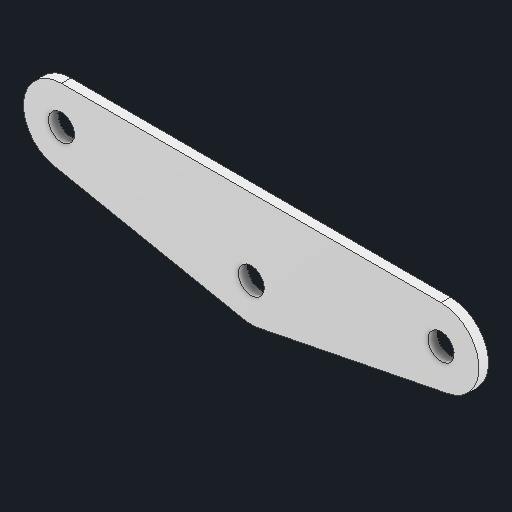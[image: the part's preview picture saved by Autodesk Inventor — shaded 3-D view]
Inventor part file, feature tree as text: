
AUTODESK INVENTOR PART (.ipt)
format: ipt  version: 2025 (Build 290162000, 162)  size: 99,840 bytes
history: native  units: in
note: dims shown in document units (in); Inventor stores cm internally (conversion verified against a paired STEP export)
features: other x3, extrude x1, sketch x1
ambient origin geometry x8: Origin, YZ Plane, XZ Plane, XY Plane, X Axis, Y Axis, Z Axis, Center Point
bodies: Solid1 (feature_tree)
feature tree (5):
  other  "Blocks"
  extrude  "Extrusion1"  [1 undecoded]
  sketch  "Sketch1"  dims[d1=0.0625in d2=0.0in]
  other  "main"
  other  "main:1"
note: 1 required parameter value undecoded (feature->parameter linkage not recoverable at this tier; creation-order binding heuristic only, values carry confidence <= 0.55)
